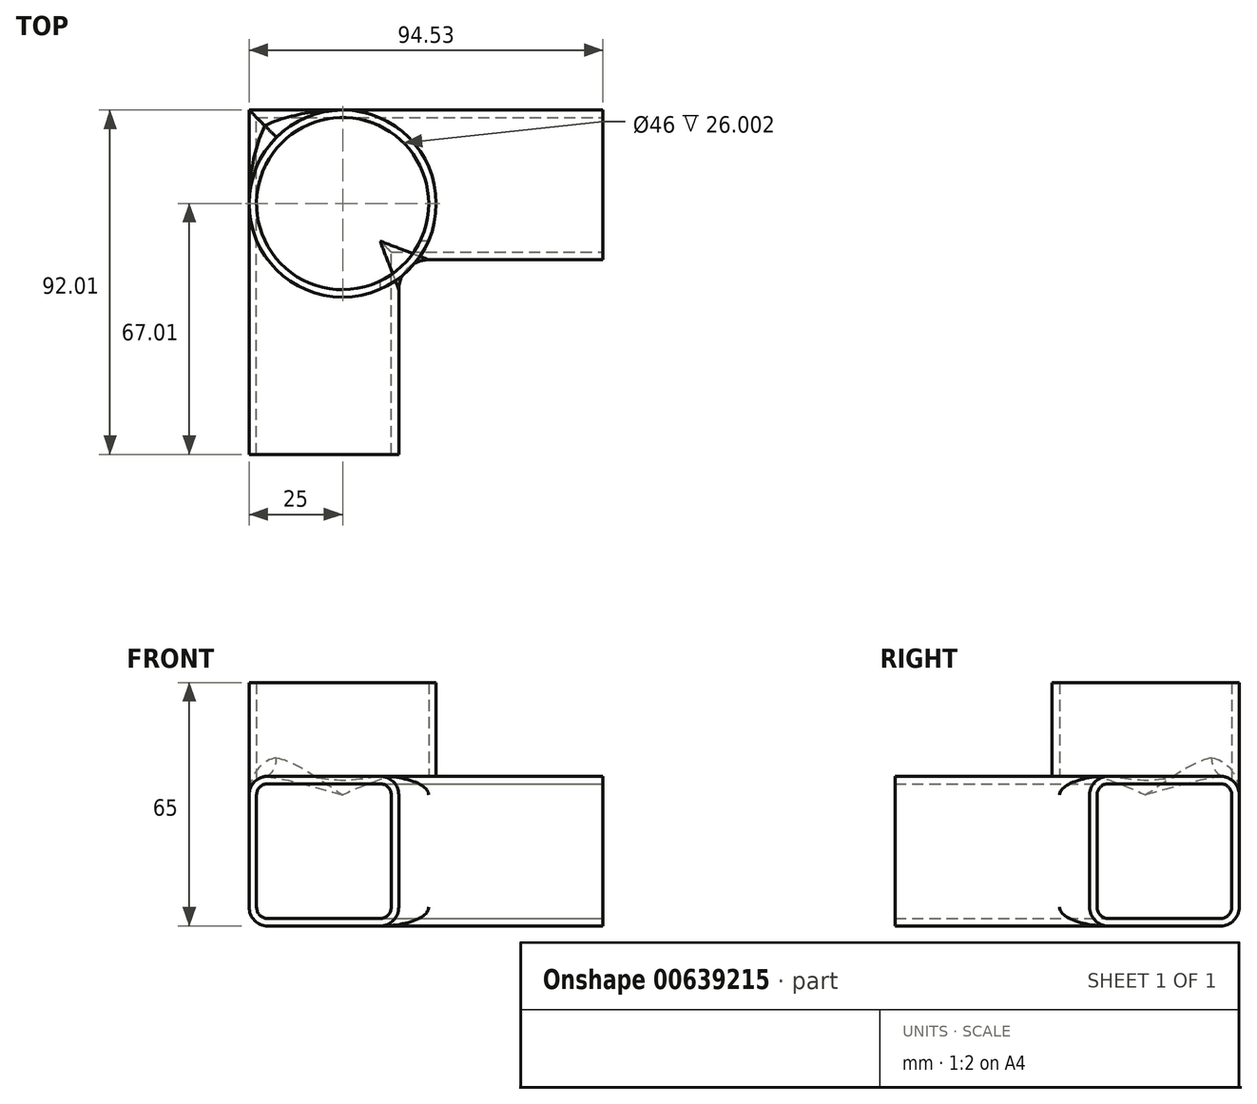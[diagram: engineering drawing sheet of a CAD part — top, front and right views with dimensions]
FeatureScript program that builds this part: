
annotation { "Feature Type Name" : "Feature", "Feature Type Description" : "" }
export const myFeature = defineFeature(function(context is Context, id is Id, definition is map)
    precondition{}
    {
        {
            var Q0;
            Q0=qCreatedBy(makeId("Top.planeOp"),FACE);
            var sketch = newSketch(context, id + "F0", { "sketchPlane" : qUnion([Q0])});
            skLineSegment(sketch, "E0", {"start": v(0, -92) * mm, "end": v(0, 0) * mm});
            skLineSegment(sketch, "E1", {"start": v(0, 0) * mm, "end": v(94.53, 0) * mm});
            skLineSegment(sketch, "E2", {"start": v(94.53, 0) * mm, "end": v(94.53, -40) * mm});
            skLineSegment(sketch, "E3", {"start": v(94.53, -40) * mm, "end": v(40, -40) * mm});
            skLineSegment(sketch, "E4", {"start": v(40, -40) * mm, "end": v(40, -92) * mm});
            skLineSegment(sketch, "E5", {"start": v(40, -92) * mm, "end": v(0, -92) * mm});
            skSolve(sketch);
        }
        {
            var Q0;
            Q0=makeQuery(id+"F0.imprint","IMPRINT",FACE,{"disambiguationData":[TD([[makeQuery(id+"F0.imprint","IMPRINT",EDGE,{"derivedFrom":sQuery(id+"F0.wireOp",EDGE,"E0")}),-1.0]])]});
            extrude(context, id + "F1", {"entities" : qUnion([Q0]), "endBound" : BoundingType.SYMMETRIC, "depth" : 40 * mm, "offsetDistance" : 25 * mm});
        }
        {
            var Q0;
            Q0=makeQuery(id+"F1.opExtrude","CAP_EDGE",EDGE,{"disambiguationData":[OSD([sQuery(id+"F0.wireOp",EDGE,"E4")])],"isStart":false});
            var Q1;
            Q1=makeQuery(id+"F1.opExtrude","CAP_EDGE",EDGE,{"disambiguationData":[OSD([sQuery(id+"F0.wireOp",EDGE,"E0")])],"isStart":false});
            var Q2;
            Q2=makeQuery(id+"F1.opExtrude","CAP_EDGE",EDGE,{"disambiguationData":[OSD([sQuery(id+"F0.wireOp",EDGE,"E4")])],"isStart":true});
            var Q3;
            Q3=makeQuery(id+"F1.opExtrude","CAP_EDGE",EDGE,{"disambiguationData":[OSD([sQuery(id+"F0.wireOp",EDGE,"E3")])],"isStart":false});
            var Q4;
            Q4=makeQuery(id+"F1.opExtrude","CAP_EDGE",EDGE,{"disambiguationData":[OSD([sQuery(id+"F0.wireOp",EDGE,"E1")])],"isStart":false});
            var Q5;
            Q5=makeQuery(id+"F1.opExtrude","CAP_EDGE",EDGE,{"disambiguationData":[OSD([sQuery(id+"F0.wireOp",EDGE,"E1")])],"isStart":true});
            var Q6;
            Q6=makeQuery(id+"F1.opExtrude","CAP_EDGE",EDGE,{"disambiguationData":[OSD([sQuery(id+"F0.wireOp",EDGE,"E3")])],"isStart":true});
            var Q7;
            Q7=makeQuery(id+"F1.opExtrude","CAP_EDGE",EDGE,{"disambiguationData":[OSD([sQuery(id+"F0.wireOp",EDGE,"E0")])],"isStart":true});
            fillet(context, id + "F2", {"entities" : qUnion([Q0, Q1, Q2, Q3, Q4, Q5, Q6, Q7]), "radius" : 5 * mm, "tangentPropagation" : true, "allowEdgeOverflow" : false});
        }
        {
            var Q0;
            Q0=makeQuery(id+"F1.opExtrude","SWEPT_FACE",FACE,{"disambiguationData":[OSD([sQuery(id+"F0.wireOp",EDGE,"E5")])]});
            var Q1;
            Q1=makeQuery(id+"F1.opExtrude","SWEPT_FACE",FACE,{"disambiguationData":[OSD([sQuery(id+"F0.wireOp",EDGE,"E2")])]});
            shell(context, id + "F3", {"entities" : qUnion([Q0, Q1]), "thickness" : 2 * mm});
        }
        {
            var Q0;
            Q0=makeQuery(id+"F1.opExtrude","CAP_FACE",FACE,{"disambiguationData":[OSD([sQuery(id+"F0.wireOp",EDGE,"E0"),sQuery(id+"F0.wireOp",EDGE,"E1"),sQuery(id+"F0.wireOp",EDGE,"E2"),sQuery(id+"F0.wireOp",EDGE,"E3"),sQuery(id+"F0.wireOp",EDGE,"E4"),sQuery(id+"F0.wireOp",EDGE,"E5")])],"isStart":false});
            var sketch = newSketch(context, id + "F4", { "sketchPlane" : qUnion([Q0])});
            skLineSegment(sketch, "E6", {"start": v(0, 0) * mm, "end": v(68.88, -68.88) * mm});
            skCircle(sketch, "E7", {"center": v(25, -25) * mm, "radius": 25 * mm});
            skSolve(sketch);
        }
        {
            var Q0;
            Q0=makeQuery(id+"F2.opFillet","BLEND_EDGE",EDGE,{"blendedFrom":[makeQuery(id+"F1.opExtrude","CAP_EDGE",EDGE,{"disambiguationData":[OSD([sQuery(id+"F0.wireOp",EDGE,"E3")])],"isStart":false}),makeQuery(id+"F1.opExtrude","CAP_EDGE",EDGE,{"disambiguationData":[OSD([sQuery(id+"F0.wireOp",EDGE,"E4")])],"isStart":false})],"blendedInto":[]});
            fillet(context, id + "F5", {"entities" : qUnion([Q0]), "radius" : 8 * mm, "tangentPropagation" : true, "allowEdgeOverflow" : false});
        }
        {
            var Q0;
            Q0 = qSketchRegion(id + "F4", true);
            var Q1;
            Q1=sQuery(id+"F4.wireOp",EDGE,"E7");
            extrude(context, id + "F6", {"entities" : qUnion([Q0]), "surfaceEntities" : qUnion([Q1]), "depth" : 25 * mm, "offsetDistance" : 25 * mm});
        }
        {
            var Q0;
            Q0=makeQuery(id+"F6.opExtrude","CAP_FACE",FACE,{"disambiguationData":[OSD([sQuery(id+"F4.wireOp",EDGE,"E7")])],"isStart":false});
            var Q1;
            Q1=makeQuery(id+"F6.opExtrude","CAP_FACE",FACE,{"disambiguationData":[OSD([sQuery(id+"F4.wireOp",EDGE,"E7")])],"isStart":true});
            shell(context, id + "F7", {"entities" : qUnion([Q0, Q1]), "thickness" : 2 * mm});
        }
        {
            var Q0;
            Q0=makeQuery(id+"F1.opExtrude","SWEPT_BODY",BODY,{"disambiguationData":[OSD([sQuery(id+"F0.wireOp",EDGE,"E0"),sQuery(id+"F0.wireOp",EDGE,"E1"),sQuery(id+"F0.wireOp",EDGE,"E2"),sQuery(id+"F0.wireOp",EDGE,"E3"),sQuery(id+"F0.wireOp",EDGE,"E4"),sQuery(id+"F0.wireOp",EDGE,"E5")])]});
            var Q1;
            Q1=makeQuery(id+"F6.opExtrude","SWEPT_BODY",BODY,{"disambiguationData":[OSD([sQuery(id+"F4.wireOp",EDGE,"E7")])]});
            booleanBodies(context, id + "F8", {"operationType" : BooleanOperationType.UNION, "tools" : qUnion([Q0, Q1])});
        }
        {
            var Q0;
            {var subQ0=sQuery(id+"F0.wireOp",EDGE,"E0");var subQ1=sQuery(id+"F4.wireOp",EDGE,"E7");Q0=makeQuery(id+"F8.opBoolean","SPLIT",FACE,{"disambiguationData":[TD([makeQuery(id+"F2.opFillet","BLEND_FACE",FACE,{"disambiguationData":[OSD([subQ0]),TDD([makeQuery(id+"F1.opExtrude","CAP_EDGE",EDGE,{"disambiguationData":[OSD([subQ0])],"isStart":false})])]})])],"derivedFrom":makeQuery(id+"F6.opExtrude","CAP_FACE",FACE,{"disambiguationData":[OSD([subQ1])],"isStart":true})});}
            var Q1;
            {var subQ0=sQuery(id+"F0.wireOp",EDGE,"E1");var subQ1=sQuery(id+"F4.wireOp",EDGE,"E7");Q1=makeQuery(id+"F8.opBoolean","SPLIT",FACE,{"disambiguationData":[TD([makeQuery(id+"F2.opFillet","BLEND_FACE",FACE,{"disambiguationData":[OSD([subQ0]),TDD([makeQuery(id+"F1.opExtrude","CAP_EDGE",EDGE,{"disambiguationData":[OSD([subQ0])],"isStart":false})])]})])],"derivedFrom":makeQuery(id+"F6.opExtrude","CAP_FACE",FACE,{"disambiguationData":[OSD([subQ1])],"isStart":true})});}
            extrude(context, id + "F9", {"entities" : qUnion([Q0, Q1]), "operationType" : NewBodyOperationType.ADD, "endBound" : BoundingType.UP_TO_NEXT, "depth" : 25 * mm, "offsetDistance" : 25 * mm});
        }
        {
            var Q0;
            {var subQ0=sQuery(id+"F4.wireOp",EDGE,"E7");var subQ1=makeQuery(id+"F6.opExtrude","SWEPT_FACE",FACE,{"disambiguationData":[OSD([subQ0])]});var subQ2=sQuery(id+"F0.wireOp",EDGE,"E1");var subQ3=sQuery(id+"F0.wireOp",EDGE,"E0");var subQ4=makeQuery(id+"F1.opExtrude","CAP_FACE",FACE,{"disambiguationData":[OSD([subQ3,subQ2,sQuery(id+"F0.wireOp",EDGE,"E2"),sQuery(id+"F0.wireOp",EDGE,"E3"),sQuery(id+"F0.wireOp",EDGE,"E4"),sQuery(id+"F0.wireOp",EDGE,"E5")])],"isStart":false});Q0=makeQuery(id+"F8.opBoolean","SPLIT",EDGE,{"disambiguationData":[topologyDisambiguationEdgeConnected([subQ4,subQ1]),TD([subQ4,makeQuery(id+"F2.opFillet","BLEND_FACE",FACE,{"disambiguationData":[OSD([subQ3]),TDD([makeQuery(id+"F1.opExtrude","CAP_EDGE",EDGE,{"disambiguationData":[OSD([subQ3])],"isStart":false})])]}),makeQuery(id+"F2.opFillet","BLEND_FACE",FACE,{"disambiguationData":[OSD([subQ2]),TDD([makeQuery(id+"F1.opExtrude","CAP_EDGE",EDGE,{"disambiguationData":[OSD([subQ2])],"isStart":false})])]}),subQ1,makeQuery(id+"F6.opExtrude","CAP_FACE",FACE,{"disambiguationData":[OSD([subQ0])],"isStart":true})])],"derivedFrom":makeQuery(id+"F6.opExtrude","CAP_EDGE",EDGE,{"disambiguationData":[OSD([subQ0])],"isStart":true})});}
            var Q1;
            {var subQ0=sQuery(id+"F0.wireOp",EDGE,"E0");var subQ1=sQuery(id+"F4.wireOp",EDGE,"E7");var subQ2=makeQuery(id+"F6.opExtrude","CAP_FACE",FACE,{"disambiguationData":[OSD([subQ1])],"isStart":true});var subQ3=makeQuery(id+"F6.opExtrude","SWEPT_FACE",FACE,{"disambiguationData":[OSD([subQ1])]});Q1=makeQuery(id+"F9.opExtrude","CAP_EDGE",EDGE,{"disambiguationData":[OSD([subQ1]),TDD([makeQuery(id+"F8.opBoolean","SPLIT",EDGE,{"disambiguationData":[topologyDisambiguationEdgeConnected([subQ3,subQ2]),TD([makeQuery(id+"F2.opFillet","BLEND_FACE",FACE,{"disambiguationData":[OSD([subQ0]),TDD([makeQuery(id+"F1.opExtrude","CAP_EDGE",EDGE,{"disambiguationData":[OSD([subQ0])],"isStart":false})])]})])],"derivedFrom":makeQuery(id+"F6.opExtrude","CAP_EDGE",EDGE,{"disambiguationData":[OSD([subQ1])],"isStart":true})})]),OD(1.0)],"isStart":false});}
            var Q2;
            {var subQ0=sQuery(id+"F0.wireOp",EDGE,"E0");var subQ1=sQuery(id+"F4.wireOp",EDGE,"E7");var subQ2=makeQuery(id+"F6.opExtrude","CAP_FACE",FACE,{"disambiguationData":[OSD([subQ1])],"isStart":true});var subQ3=makeQuery(id+"F6.opExtrude","SWEPT_FACE",FACE,{"disambiguationData":[OSD([subQ1])]});Q2=makeQuery(id+"F9.opExtrude","CAP_EDGE",EDGE,{"disambiguationData":[OSD([subQ1]),TDD([makeQuery(id+"F8.opBoolean","SPLIT",EDGE,{"disambiguationData":[topologyDisambiguationEdgeConnected([subQ3,subQ2]),TD([makeQuery(id+"F2.opFillet","BLEND_FACE",FACE,{"disambiguationData":[OSD([subQ0]),TDD([makeQuery(id+"F1.opExtrude","CAP_EDGE",EDGE,{"disambiguationData":[OSD([subQ0])],"isStart":false})])]})])],"derivedFrom":makeQuery(id+"F6.opExtrude","CAP_EDGE",EDGE,{"disambiguationData":[OSD([subQ1])],"isStart":true})})]),OD(0.0)],"isStart":false});}
            var Q3;
            {var subQ0=sQuery(id+"F0.wireOp",EDGE,"E1");var subQ1=sQuery(id+"F4.wireOp",EDGE,"E7");var subQ2=makeQuery(id+"F6.opExtrude","CAP_FACE",FACE,{"disambiguationData":[OSD([subQ1])],"isStart":true});var subQ3=makeQuery(id+"F6.opExtrude","SWEPT_FACE",FACE,{"disambiguationData":[OSD([subQ1])]});Q3=makeQuery(id+"F9.opExtrude","CAP_EDGE",EDGE,{"disambiguationData":[OSD([subQ1]),TDD([makeQuery(id+"F8.opBoolean","SPLIT",EDGE,{"disambiguationData":[topologyDisambiguationEdgeConnected([subQ3,subQ2]),TD([makeQuery(id+"F2.opFillet","BLEND_FACE",FACE,{"disambiguationData":[OSD([subQ0]),TDD([makeQuery(id+"F1.opExtrude","CAP_EDGE",EDGE,{"disambiguationData":[OSD([subQ0])],"isStart":false})])]})])],"derivedFrom":makeQuery(id+"F6.opExtrude","CAP_EDGE",EDGE,{"disambiguationData":[OSD([subQ1])],"isStart":true})})]),OD(1.0)],"isStart":false});}
            fillet(context, id + "F10", {"entities" : qUnion([Q0, Q1, Q2, Q3]), "radius" : 5 * mm, "tangentPropagation" : true, "allowEdgeOverflow" : false});
        }
    });
